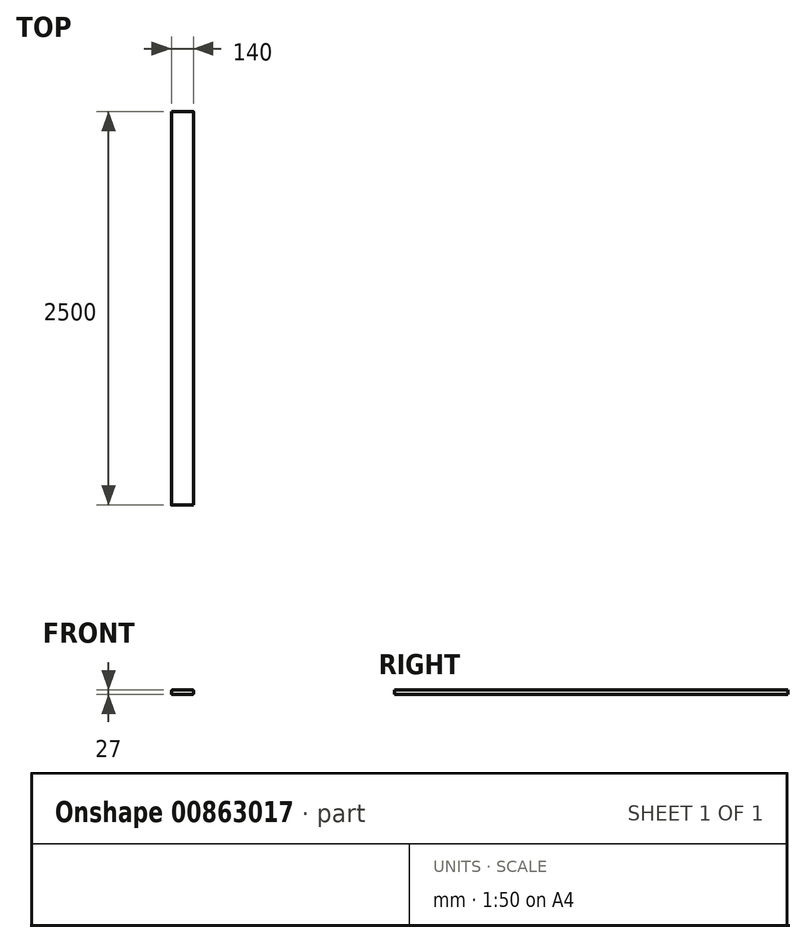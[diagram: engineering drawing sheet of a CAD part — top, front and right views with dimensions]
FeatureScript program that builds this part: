
annotation { "Feature Type Name" : "Feature", "Feature Type Description" : "" }
export const myFeature = defineFeature(function(context is Context, id is Id, definition is map)
    precondition{}
    {
        {
            var Q0;
            Q0=qCreatedBy(makeId("Front.planeOp"),FACE);
            var sketch = newSketch(context, id + "F0", { "sketchPlane" : qUnion([Q0])});
            skLineSegment(sketch, "E0.bottom", {"start": v(0, 0) * mm, "end": v(-140, 0) * mm});
            skLineSegment(sketch, "E0.top", {"start": v(0, 27) * mm, "end": v(-140, 27) * mm});
            skLineSegment(sketch, "E0.left", {"start": v(0, 0) * mm, "end": v(0, 27) * mm});
            skLineSegment(sketch, "E0.right", {"start": v(-140, 0) * mm, "end": v(-140, 27) * mm});
            skSolve(sketch);
        }
        {
            var Q0;
            Q0 = qSketchRegion(id + "F0", true);
            extrude(context, id + "F1", {"entities" : qUnion([Q0]), "depth" : 2500 * mm, "offsetDistance" : 25 * mm});
        }
        {
            var Q0;
            Q0=makeQuery(id+"F1.opExtrude","SWEPT_EDGE",EDGE,{"disambiguationData":[OSD([sQuery(id+"F0.wireOp",EDGE,"E0.top"),sQuery(id+"F0.wireOp",EDGE,"E0.left")])]});
            var Q1;
            Q1=makeQuery(id+"F1.opExtrude","SWEPT_EDGE",EDGE,{"disambiguationData":[OSD([sQuery(id+"F0.wireOp",EDGE,"E0.bottom"),sQuery(id+"F0.wireOp",EDGE,"E0.left")])]});
            var Q2;
            Q2=makeQuery(id+"F1.opExtrude","SWEPT_EDGE",EDGE,{"disambiguationData":[OSD([sQuery(id+"F0.wireOp",EDGE,"E0.top"),sQuery(id+"F0.wireOp",EDGE,"E0.right")])]});
            var Q3;
            Q3=makeQuery(id+"F1.opExtrude","SWEPT_EDGE",EDGE,{"disambiguationData":[OSD([sQuery(id+"F0.wireOp",EDGE,"E0.bottom"),sQuery(id+"F0.wireOp",EDGE,"E0.right")])]});
            fillet(context, id + "F2", {"entities" : qUnion([Q0, Q1, Q2, Q3]), "radius" : 5 * mm, "tangentPropagation" : true, "allowEdgeOverflow" : false});
        }
    });
